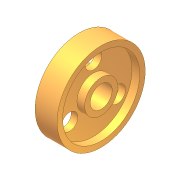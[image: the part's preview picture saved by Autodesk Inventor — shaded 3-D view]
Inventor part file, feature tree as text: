
AUTODESK INVENTOR PART (.ipt)
format: ipt  version: unknown  size: 209,920 bytes
history: native  units: in
note: dims shown in document units (in); Inventor stores cm internally (conversion verified against a paired STEP export)
features: sketch x2, revolve x1, extrude x1, pattern_circular x1
ambient origin geometry x8: Origin, YZ Plane, XZ Plane, XY Plane, X Axis, Y Axis, Z Axis, Center Point
feature tree (5):
  revolve  "Revolution1"  [1 undecoded]
  extrude  "Extrusion4"  Depth=0.0197in
  pattern_circular  "Circular Pattern4"  [2 undecoded]
  sketch  "Sketch1"  dims[d0=0.1575in d2=0.2756in d4=0.0394in]
  sketch  "Sketch6"  dims[d5=90.0deg d24=0.0197in d25=0.0197in d34=0.0118in d35=0.0394in d46=0.0in d51=0.0394in d54=0.0984in d55=0.0591in d56=0.3937in d57=0.0in d58=1.1811in d59=360.0deg]
note: 3 required parameter values undecoded (feature->parameter linkage not recoverable at this tier; creation-order binding heuristic only, values carry confidence <= 0.55)